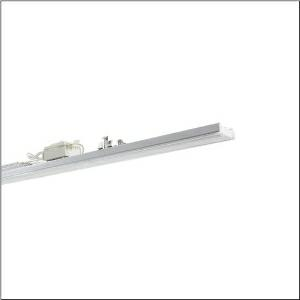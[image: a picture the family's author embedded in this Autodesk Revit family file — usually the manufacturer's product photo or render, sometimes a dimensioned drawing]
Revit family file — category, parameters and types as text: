
# Revit family: licross_21_recessed_mo_52tl11dn4axg3s4
name_source: partatom
category: Lighting Fixtures
units: mm (PartAtom-declared; Revit-internal decimal feet)

## family parameters
Cut with Voids When Loaded = No
Host = Face
Light Source = No
Part Type = Normal
Room Calculation Point = No
Round Connector Dimension = Use Diameter
Shared = No

## types (1)
- --- (1 x LED, 930 lm, 6.7 W, 4000K)
    Apparent Load = 7 VA
    CIE Flux Codes = 89 96 99 100 100
    Color Rendering = 80
    Color Temperature = 4000K
    Default Elevation = 1800 mm
    Description = Licross 21 Recessed MO, luminaire insert, of sheet steel, galvanised, coil coated, white, length: 1.500mm, width: 66mm, height: 67mm, LED rated luminous flux: 10.120lm, light colour: 840, SDCM (Standard Deviation of Colour Matching)MacAdam ≤ 3 SDCM (initial), control gear: DALI 2, with plug, 6-pole, with phase selection, for trunking rail, 9 or 11-core, mains connection: 220..240V, AC, 50/60Hz, rated input power: 62W, for emergency light function, internal wiring halogen-free, for trunking rail, 9-/11-core, converter,control gear: single battery element, battery: LiFePO4, 9Ah, primary optical cover: cover, of PMMA, light emission: direct distribution, primary light characteristic: symmetric, protection rating (complete): IP40, insulation class (complete): insulation class I (protective earthing), certification: CE, UKCA, protection symbol: D if used in an environment without relevant dust loads with corresponding accessories, impact resistance: IK06, permissible ambient temperature for indoor applications: +5..+35°C, standard: EN 60598-2-22, corresponds to IFS (International Featured Standards) requirements for safety and quality in the food industry, reducing of maximum allowable ambient temperature of 5°C with ceiling mounting, LABS conformity tested according to VDMA 24364:2018-05, The light source and the operating device comply with the requirements of the Ecodesign Regulation (EU) 2019/2020 and are replaceable in accordance with this regulation, packaging unit: 1 piece
    Height = 58 mm
    Lamp = 1 x LED
    Lamp Light Flux = 930 lm
    Lamp Power = 6.7 W
    Lamp count = 1
    Length = 1500 mm
    Luminous efficacy = 139 lm/W
    Manufacturer = Siteco
    ModVariant = No
    Model = 52TL11DN4AXG3S4
    Mounting Place = Ceiling
    Mounting Type = Pendant
    Number of Poles = 1
    OnlyDefault = Yes
    Power Factor = 1
    Product Name = Licross 21 Recessed MO
    Product group = luminaire insert | ceiling pendant
    ProductGroupID = 901
    Protection Class = Protection class I
    Protection Degree = IP 40
    RLX_Detail_Level = 1
    RLX_Emergency_Light_Flux = 0 lm
    RLX_Emergency_Type = 0
    RLX_Emergency_Type_DB = No
    RlxData = <blob elided: 25181 chars, md5=0396c9cb>
    Socket = socket
    Standby Power = 0 W
    System Light Flux = 930 lm
    System Power = 7 W
    Type Comments = : emergency light operation: 3 h
    Type Image = l_1296930.jpg
    URL = http://relux.com
    VarID = @adj_110573
    Voltage = 0 V
    Weight = 0.00 kg
    Width = 66 mm

## geometry (parser evidence)
native form markers: Blend x4, Sweep x9
no freeform markers — native parametric forms only
